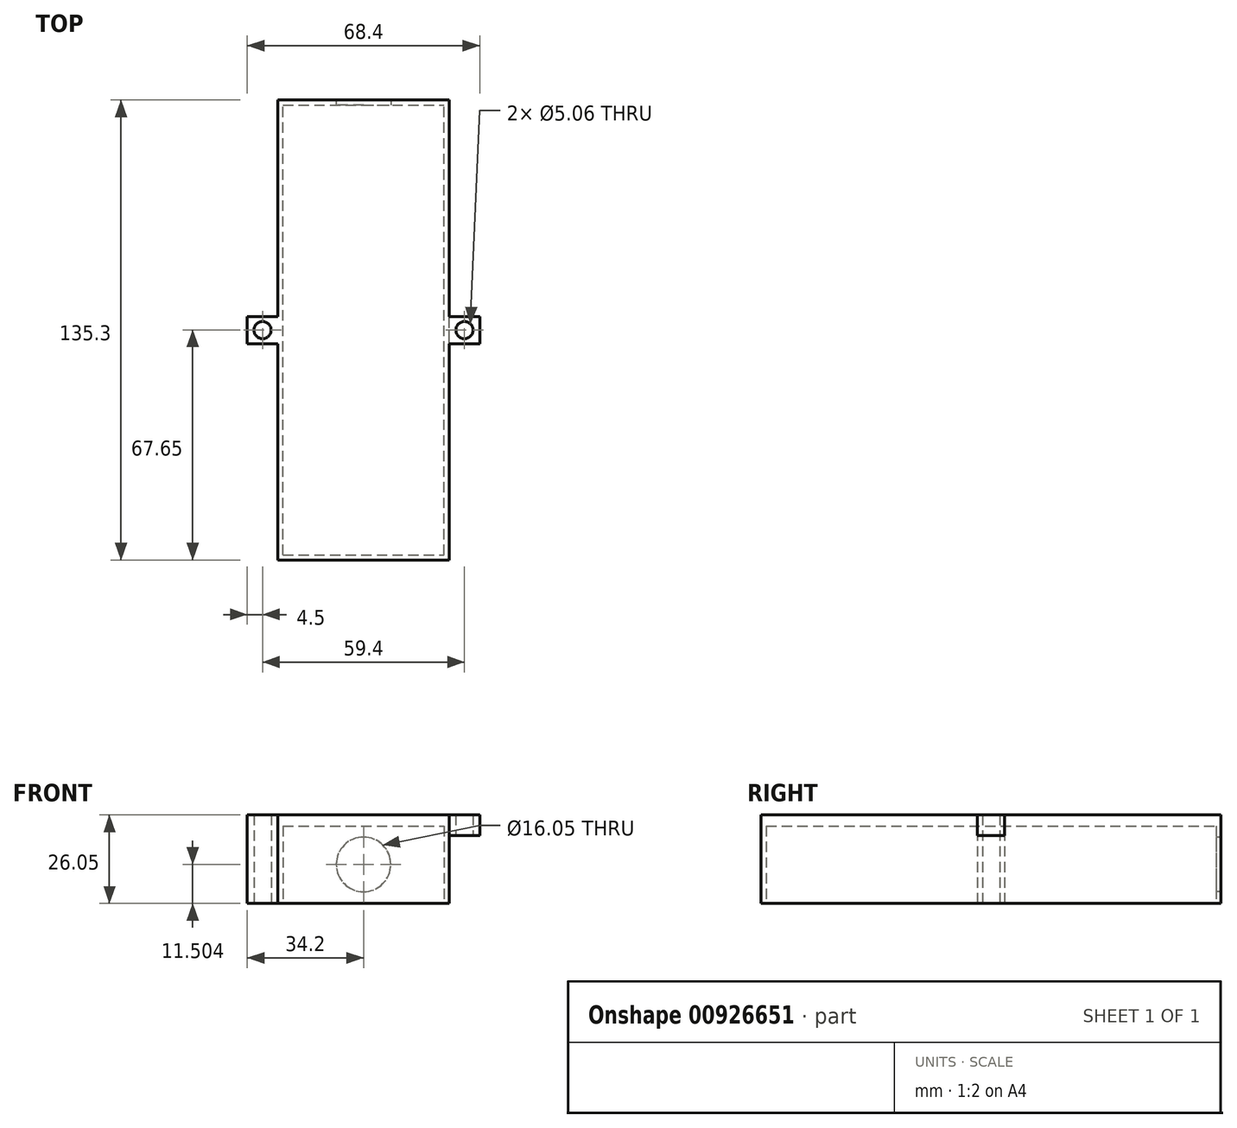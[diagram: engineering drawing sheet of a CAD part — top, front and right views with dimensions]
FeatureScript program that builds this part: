
annotation { "Feature Type Name" : "Feature", "Feature Type Description" : "" }
export const myFeature = defineFeature(function(context is Context, id is Id, definition is map)
    precondition{}
    {
        {
            var Q0;
            Q0=qCreatedBy(makeId("Top.planeOp"),FACE);
            var sketch = newSketch(context, id + "F0", { "sketchPlane" : qUnion([Q0])});
            skLineSegment(sketch, "E0.bottom", {"start": v(25.2, -67.65) * mm, "end": v(-25.2, -67.65) * mm});
            skLineSegment(sketch, "E0.top", {"start": v(25.2, 67.65) * mm, "end": v(-25.2, 67.65) * mm});
            skLineSegment(sketch, "E0.left", {"start": v(25.2, -67.65) * mm, "end": v(25.2, -12.55) * mm});
            skLineSegment(sketch, "E0.right", {"start": v(-25.2, -67.65) * mm, "end": v(-25.2, -4) * mm});
            skPoint(sketch, "E0.middle", {"position": v(0, 0) * mm});
            skLineSegment(sketch, "E1.trimOffspring", {"start": v(25.2, 4) * mm, "end": v(25.2, 67.65) * mm});
            skPoint(sketch, "E2.end.orphan", {"position": v(0, -67.65) * mm});
            skPoint(sketch, "E3.end.orphan", {"position": v(0, 67.65) * mm});
            skLineSegment(sketch, "E4.trimOffspring", {"start": v(-25.2, 4) * mm, "end": v(-25.2, 67.65) * mm});
            skCircle(sketch, "E5", {"center": v(29.7, 0) * mm, "radius": 2.53 * mm});
            skPoint(sketch, "E6.center.orphan", {"position": v(25.2, 0) * mm});
            skLineSegment(sketch, "E7.bottom", {"start": v(25.2, 4) * mm, "end": v(34.2, 4) * mm});
            skLineSegment(sketch, "E7.top", {"start": v(25.2, -4) * mm, "end": v(34.2, -4) * mm});
            skLineSegment(sketch, "E7.left", {"start": v(25.2, -4) * mm, "end": v(25.2, -12.55) * mm});
            skLineSegment(sketch, "E7.right", {"start": v(34.2, 4) * mm, "end": v(34.2, -4) * mm});
            skLineSegment(sketch, "E8", {"start": v(0, 67.65) * mm, "end": v(0, -67.65) * mm, "construction": true});
            skLineSegment(sketch, "E9.MirrorCS", {"start": v(-25.2, 4) * mm, "end": v(-34.2, 4) * mm});
            skLineSegment(sketch, "E10.MirrorCS", {"start": v(-34.2, 4) * mm, "end": v(-34.2, -4) * mm});
            skLineSegment(sketch, "E11.MirrorCS", {"start": v(-25.2, -4) * mm, "end": v(-34.2, -4) * mm});
            skCircle(sketch, "E12.MirrorC", {"center": v(-29.7, 0) * mm, "radius": 2.53 * mm});
            skLineSegment(sketch, "E13", {"start": v(25.2, 0) * mm, "end": v(34.2, 0) * mm, "construction": true});
            skPoint(sketch, "E14.end.orphan", {"position": v(29.7, 4) * mm});
            skLineSegment(sketch, "E15.left", {"start": v(25.2, -4) * mm, "end": v(25.2, 4) * mm});
            skLineSegment(sketch, "E15.right", {"start": v(34.2, -4) * mm, "end": v(34.2, 4) * mm});
            skLineSegment(sketch, "E16.bottom", {"start": v(-34.2, -4) * mm, "end": v(-25.2, -4) * mm});
            skLineSegment(sketch, "E16.top", {"start": v(-34.2, 4) * mm, "end": v(-25.2, 4) * mm});
            skLineSegment(sketch, "E16.left", {"start": v(-34.2, -4) * mm, "end": v(-34.2, 4) * mm});
            skLineSegment(sketch, "E16.right", {"start": v(-25.2, -4) * mm, "end": v(-25.2, 4) * mm});
            skSolve(sketch);
        }
        {
            var Q0;
            Q0 = qSketchRegion(id + "F0", true);
            extrude(context, id + "F1", {"entities" : qUnion([Q0]), "depth" : 26.05 * mm, "offsetDistance" : 25 * mm});
        }
        {
            var Q0;
            Q0=qCreatedBy(makeId("Top.planeOp"),FACE);
            var sketch = newSketch(context, id + "F2", { "sketchPlane" : qUnion([Q0])});
            skLineSegment(sketch, "E17.bottom", {"start": v(-23.65, -66.15) * mm, "end": v(23.65, -66.15) * mm});
            skLineSegment(sketch, "E17.top", {"start": v(-23.65, 66.15) * mm, "end": v(23.65, 66.15) * mm});
            skLineSegment(sketch, "E17.left", {"start": v(-23.65, -66.15) * mm, "end": v(-23.65, 66.15) * mm});
            skLineSegment(sketch, "E17.right", {"start": v(23.65, -66.15) * mm, "end": v(23.65, 66.15) * mm});
            skPoint(sketch, "E17.middle", {"position": v(0, 0) * mm});
            skSolve(sketch);
        }
        {
            var Q0;
            Q0 = qSketchRegion(id + "F2", true);
            extrude(context, id + "F3", {"entities" : qUnion([Q0]), "operationType" : NewBodyOperationType.REMOVE, "depth" : 22.75 * mm, "offsetDistance" : 25 * mm});
        }
        {
            var Q0;
            Q0=makeQuery(id+"F0.imprint","IMPRINT",FACE,{"disambiguationData":[TD([[makeQuery(id+"F0.imprint","IMPRINT",EDGE,{"derivedFrom":sQuery(id+"F0.wireOp",EDGE,"E5")}),-1.0]])]});
            extrude(context, id + "F4", {"entities" : qUnion([Q0]), "operationType" : NewBodyOperationType.ADD, "depth" : 15 * mm, "offsetDistance" : 25 * mm});
        }
        {
            var Q0;
            Q0=makeQuery(id+"F0.imprint","IMPRINT",FACE,{"disambiguationData":[TD([[makeQuery(id+"F0.imprint","IMPRINT",EDGE,{"derivedFrom":sQuery(id+"F0.wireOp",EDGE,"E5")}),-1.0]])]});
            extrude(context, id + "F5", {"entities" : qUnion([Q0]), "operationType" : NewBodyOperationType.REMOVE, "depth" : 20 * mm, "offsetDistance" : 25 * mm});
        }
        {
            var Q0;
            Q0=makeQuery(id+"F0.imprint","IMPRINT",FACE,{"disambiguationData":[TD([[makeQuery(id+"F0.imprint","IMPRINT",EDGE,{"derivedFrom":sQuery(id+"F0.wireOp",EDGE,"E12.MirrorC")}),1.0]])]});
            extrude(context, id + "F6", {"entities" : qUnion([Q0]), "operationType" : NewBodyOperationType.REMOVE, "depth" : 20 * mm, "offsetDistance" : 25 * mm});
        }
        {
            var Q0;
            Q0=qCreatedBy(makeId("Front.planeOp"),FACE);
            var sketch = newSketch(context, id + "F7", { "sketchPlane" : qUnion([Q0])});
            skPoint(sketch, "E18", {"position": v(0, 11.5) * mm});
            skCircle(sketch, "E19", {"center": v(0, 11.5) * mm, "radius": 8.02 * mm});
            skSolve(sketch);
        }
        {
            var Q0;
            Q0 = qSketchRegion(id + "F7", true);
            extrude(context, id + "F8", {"entities" : qUnion([Q0]), "operationType" : NewBodyOperationType.REMOVE, "oppositeDirection" : true, "depth" : 100 * mm, "offsetDistance" : 25 * mm});
        }
    });
